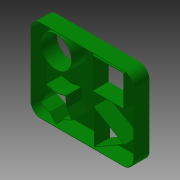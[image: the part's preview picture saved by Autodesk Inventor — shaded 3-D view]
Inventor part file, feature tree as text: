
AUTODESK INVENTOR PART (.ipt)
format: ipt  version: 2015 (Build 190159000, 159)  size: 189,440 bytes
history: native  units: in
note: dims shown in document units (in); Inventor stores cm internally (conversion verified against a paired STEP export)
features: extrude x1, shell x1, sketch x1
ambient origin geometry x8: Origin, YZ Plane, XZ Plane, XY Plane, X Axis, Y Axis, Z Axis, Center Point
bodies: Solid1 (feature_tree)
feature tree (3):
  extrude  "Extrusion1"  Depth=1.975in
  shell  "Shell1"  Thickness=0.2in
  sketch  "Sketch1"  dims[d0=1.59in d1=1.975in d2=0.2in d3=0.58in d4=0.34in d5=0.49in d6=0.58in d7=0.58in d8=0.05in d9=0.2in d10=0.638in d12=0.2in d13=0.05in d15=0.638in d16=0.638in d17=0.412in d18=0.605in d19=1.9685in d21=360.0deg d23=1.9685in d25=360.0deg d27=0.363in d28=0.488in d29=0.3in d30=0.0in d31=0.01in]
